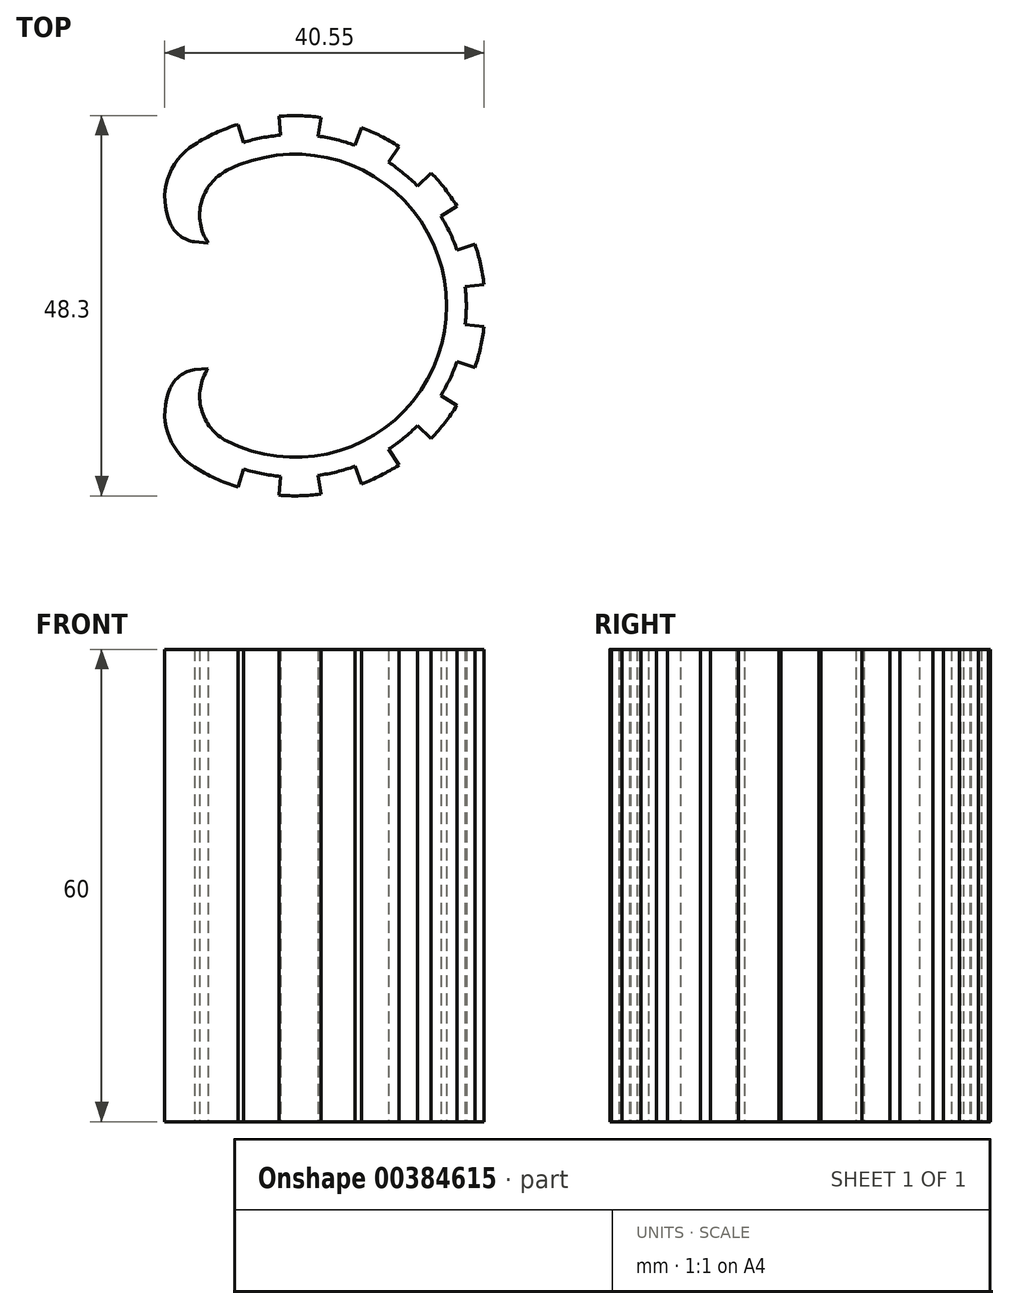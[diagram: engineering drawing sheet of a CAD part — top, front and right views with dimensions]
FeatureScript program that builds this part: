
annotation { "Feature Type Name" : "Feature", "Feature Type Description" : "" }
export const myFeature = defineFeature(function(context is Context, id is Id, definition is map)
    precondition{}
    {
        {
            var Q0;
            Q0=qCreatedBy(makeId("Top.planeOp"),FACE);
            var sketch = newSketch(context, id + "F0", { "sketchPlane" : qUnion([Q0])});
            skCircle(sketch, "E0", {"center": v(0, 0) * mm, "radius": 24.15 * mm, "construction": true});
            skCircle(sketch, "E1", {"center": v(0, 0) * mm, "radius": 19.25 * mm, "construction": true});
            skCircle(sketch, "E2", {"center": v(0, 0) * mm, "radius": 21.75 * mm, "construction": true});
            skLineSegment(sketch, "E3", {"start": v(24.15, -24.78) * mm, "end": v(24.15, 24.83) * mm, "construction": true});
            skLineSegment(sketch, "E4", {"start": v(-27.29, 0) * mm, "end": v(29.37, 0) * mm, "construction": true});
            skLineSegment(sketch, "E5.0", {"start": v(-27.29, -7.7) * mm, "end": v(29.37, -7.7) * mm, "construction": true});
            skLineSegment(sketch, "E6.0", {"start": v(-27.29, 7.7) * mm, "end": v(29.37, 7.7) * mm, "construction": true});
            skLineSegment(sketch, "E7", {"start": v(-7.9, 7.7) * mm, "end": v(-30.03, 9.64) * mm, "construction": true});
            skLineSegment(sketch, "E8", {"start": v(-9.96, -7.7) * mm, "end": v(-30.2, -9.47) * mm, "construction": true});
            skLineSegment(sketch, "E9", {"start": v(-7.25, 14.43) * mm, "end": v(-7.25, 0) * mm, "construction": true});
            skLineSegment(sketch, "E10", {"start": v(-7.25, 0) * mm, "end": v(-7.25, -27.12) * mm, "construction": true});
            skLineSegment(sketch, "E11.0", {"start": v(-16.55, -24.78) * mm, "end": v(-16.55, 24.83) * mm, "construction": true});
            skLineSegment(sketch, "E12.0", {"start": v(-11.05, -24.78) * mm, "end": v(-11.05, 24.83) * mm, "construction": true});
            skCircle(sketch, "E13", {"center": v(-8.55, 13.7) * mm, "radius": 8 * mm, "construction": true});
            skCircle(sketch, "E14", {"center": v(-12.21, 12.1) * mm, "radius": 4 * mm, "construction": true});
            skPoint(sketch, "E15", {"position": v(-11.05, 7.98) * mm});
            skCircle(sketch, "E16.MirrorC", {"center": v(-8.55, -13.7) * mm, "radius": 8 * mm, "construction": true});
            skCircle(sketch, "E17.MirrorC", {"center": v(-12.21, -12.1) * mm, "radius": 4 * mm, "construction": true});
            skArc(sketch, "E18.MirrorCS", {"start": v(-8.64, -17.2) * mm, "mid": v(-11.28, -12.96) * mm, "end": v(-11.05, -7.98) * mm, "construction": true});
            skArc(sketch, "E19", {"start": v(-8.57, 17.24) * mm, "mid": v(-11.9, 13.17) * mm, "end": v(-11.05, 7.98) * mm, "construction": true});
            skSolve(sketch);
        }
        {
            var Q0;
            Q0=qCreatedBy(makeId("Top.planeOp"),FACE);
            var sketch = newSketch(context, id + "F1", { "sketchPlane" : qUnion([Q0])});
            skLineSegment(sketch, "E20", {"start": v(0, 0) * mm, "end": v(-10.1, 32.05) * mm, "construction": true});
            skPoint(sketch, "E21.center", {"position": v(0, 0) * mm});
            skLineSegment(sketch, "E22.1.0", {"start": v(0, 0) * mm, "end": v(33.61, 0) * mm, "construction": true});
            skLineSegment(sketch, "E22.2.0", {"start": v(0, 0) * mm, "end": v(-10.1, -32.05) * mm, "construction": true});
            skSolve(sketch);
        }
        {
            var Q0;
            Q0=qCreatedBy(makeId("Top.planeOp"),FACE);
            var sketch = newSketch(context, id + "F2", { "sketchPlane" : qUnion([Q0])});
            skLineSegment(sketch, "E23", {"start": v(-6.55, 20.74) * mm, "end": v(-7.26, 23.03) * mm});
            skLineSegment(sketch, "E24.1.0", {"start": v(-1.85, 21.67) * mm, "end": v(-2.04, 24.06) * mm});
            skLineSegment(sketch, "E24.2.0", {"start": v(2.94, 21.55) * mm, "end": v(3.28, 23.93) * mm});
            skLineSegment(sketch, "E24.3.0", {"start": v(7.59, 20.38) * mm, "end": v(8.43, 22.63) * mm});
            skLineSegment(sketch, "E24.4.0", {"start": v(11.86, 18.23) * mm, "end": v(13.18, 20.23) * mm});
            skLineSegment(sketch, "E24.5.0", {"start": v(15.57, 15.19) * mm, "end": v(17.3, 16.86) * mm});
            skLineSegment(sketch, "E24.6.0", {"start": v(18.52, 11.41) * mm, "end": v(20.57, 12.66) * mm});
            skLineSegment(sketch, "E24.7.0", {"start": v(20.57, 7.08) * mm, "end": v(22.84, 7.85) * mm});
            skLineSegment(sketch, "E24.8.0", {"start": v(21.62, 2.4) * mm, "end": v(24, 2.66) * mm});
            skLineSegment(sketch, "E24.9.0", {"start": v(21.62, -2.38) * mm, "end": v(24, -2.66) * mm});
            skLineSegment(sketch, "E24.10.0", {"start": v(20.57, -7.06) * mm, "end": v(22.84, -7.85) * mm});
            skLineSegment(sketch, "E24.11.0", {"start": v(18.53, -11.4) * mm, "end": v(20.57, -12.66) * mm});
            skLineSegment(sketch, "E24.12.0", {"start": v(15.58, -15.17) * mm, "end": v(17.3, -16.86) * mm});
            skLineSegment(sketch, "E24.13.0", {"start": v(11.88, -18.22) * mm, "end": v(13.18, -20.23) * mm});
            skLineSegment(sketch, "E24.14.0", {"start": v(7.6, -20.38) * mm, "end": v(8.43, -22.63) * mm});
            skLineSegment(sketch, "E24.15.0", {"start": v(2.96, -21.55) * mm, "end": v(3.28, -23.93) * mm});
            skLineSegment(sketch, "E24.16.0", {"start": v(-1.83, -21.67) * mm, "end": v(-2.04, -24.06) * mm});
            skLineSegment(sketch, "E24.17.0", {"start": v(-6.53, -20.75) * mm, "end": v(-7.26, -23.03) * mm});
            skPoint(sketch, "E24.center", {"position": v(0, 0) * mm});
            skLineSegment(sketch, "E24.anchor1", {"start": v(0, 0) * mm, "end": v(-6.55, 20.74) * mm, "construction": true});
            skLineSegment(sketch, "E24.anchor2", {"start": v(0, 0) * mm, "end": v(-6.53, -20.75) * mm, "construction": true});
            skArc(sketch, "E25", {"start": v(19.25, 0) * mm, "mid": v(10.11, 16.38) * mm, "end": v(-8.63, 17.2) * mm});
            skArc(sketch, "E26", {"start": v(-8.63, 17.2) * mm, "mid": v(-11.9, 13.13) * mm, "end": v(-11.05, 7.98) * mm});
            skArc(sketch, "E27", {"start": v(-12.79, 20.49) * mm, "mid": v(-16.2, 16.06) * mm, "end": v(-15.87, 10.48) * mm});
            skArc(sketch, "E28", {"start": v(-15.87, 10.48) * mm, "mid": v(-14.62, 8.9) * mm, "end": v(-12.74, 8.13) * mm});
            skLineSegment(sketch, "E29", {"start": v(-12.74, 8.13) * mm, "end": v(-11.05, 7.98) * mm});
            skArc(sketch, "E30", {"start": v(-12.79, 20.49) * mm, "mid": v(-10.1, 21.93) * mm, "end": v(-7.26, 23.03) * mm});
            skArc(sketch, "E31", {"start": v(-6.55, 20.74) * mm, "mid": v(-4.23, 21.34) * mm, "end": v(-1.85, 21.67) * mm});
            skArc(sketch, "E32", {"start": v(2.94, 21.55) * mm, "mid": v(5.3, 21.1) * mm, "end": v(7.59, 20.38) * mm});
            skArc(sketch, "E33", {"start": v(3.28, 23.93) * mm, "mid": v(0.62, 24.14) * mm, "end": v(-2.04, 24.06) * mm});
            skArc(sketch, "E34", {"start": v(8.43, 22.63) * mm, "mid": v(10.88, 21.56) * mm, "end": v(13.18, 20.23) * mm});
            skArc(sketch, "E35", {"start": v(11.86, 18.23) * mm, "mid": v(13.8, 16.81) * mm, "end": v(15.57, 15.19) * mm});
            skArc(sketch, "E36", {"start": v(17.3, 16.86) * mm, "mid": v(19.05, 14.85) * mm, "end": v(20.57, 12.66) * mm});
            skArc(sketch, "E37", {"start": v(18.52, 11.41) * mm, "mid": v(19.66, 9.3) * mm, "end": v(20.57, 7.08) * mm});
            skArc(sketch, "E38", {"start": v(22.84, 7.85) * mm, "mid": v(23.56, 5.29) * mm, "end": v(24, 2.66) * mm});
            skArc(sketch, "E39", {"start": v(21.62, 2.4) * mm, "mid": v(21.72, 1.2) * mm, "end": v(21.75, 0) * mm});
            skArc(sketch, "E40.MirrorCS", {"start": v(21.62, -2.4) * mm, "mid": v(21.72, -1.2) * mm, "end": v(21.75, 0) * mm});
            skLineSegment(sketch, "E41.MirrorCS", {"start": v(21.62, -2.4) * mm, "end": v(24, -2.66) * mm});
            skArc(sketch, "E42.MirrorCS", {"start": v(22.84, -7.85) * mm, "mid": v(23.56, -5.29) * mm, "end": v(24, -2.66) * mm});
            skLineSegment(sketch, "E43.MirrorCS", {"start": v(20.57, -7.08) * mm, "end": v(22.84, -7.85) * mm});
            skArc(sketch, "E44.MirrorCS", {"start": v(18.52, -11.41) * mm, "mid": v(19.66, -9.3) * mm, "end": v(20.57, -7.08) * mm});
            skLineSegment(sketch, "E45.MirrorCS", {"start": v(18.52, -11.41) * mm, "end": v(20.57, -12.66) * mm});
            skArc(sketch, "E46.MirrorCS", {"start": v(17.3, -16.86) * mm, "mid": v(19.05, -14.85) * mm, "end": v(20.57, -12.66) * mm});
            skLineSegment(sketch, "E47.MirrorCS", {"start": v(15.57, -15.19) * mm, "end": v(17.3, -16.86) * mm});
            skArc(sketch, "E48.MirrorCS", {"start": v(11.86, -18.23) * mm, "mid": v(13.8, -16.81) * mm, "end": v(15.57, -15.19) * mm});
            skLineSegment(sketch, "E49.MirrorCS", {"start": v(11.86, -18.23) * mm, "end": v(13.18, -20.23) * mm});
            skArc(sketch, "E50.MirrorCS", {"start": v(8.43, -22.63) * mm, "mid": v(10.88, -21.56) * mm, "end": v(13.18, -20.23) * mm});
            skLineSegment(sketch, "E51.MirrorCS", {"start": v(7.59, -20.38) * mm, "end": v(8.43, -22.63) * mm});
            skArc(sketch, "E52.MirrorCS", {"start": v(2.94, -21.55) * mm, "mid": v(5.3, -21.1) * mm, "end": v(7.59, -20.38) * mm});
            skLineSegment(sketch, "E53.MirrorCS", {"start": v(2.94, -21.55) * mm, "end": v(3.28, -23.93) * mm});
            skArc(sketch, "E54.MirrorCS", {"start": v(3.28, -23.93) * mm, "mid": v(0.62, -24.14) * mm, "end": v(-2.04, -24.06) * mm});
            skLineSegment(sketch, "E55.MirrorCS", {"start": v(-1.85, -21.67) * mm, "end": v(-2.04, -24.06) * mm});
            skArc(sketch, "E56.MirrorCS", {"start": v(-6.55, -20.74) * mm, "mid": v(-4.23, -21.34) * mm, "end": v(-1.85, -21.67) * mm});
            skLineSegment(sketch, "E57.MirrorCS", {"start": v(-6.55, -20.74) * mm, "end": v(-7.26, -23.03) * mm});
            skArc(sketch, "E58.MirrorCS", {"start": v(-12.79, -20.49) * mm, "mid": v(-10.1, -21.93) * mm, "end": v(-7.26, -23.03) * mm});
            skArc(sketch, "E59.MirrorCS", {"start": v(-12.79, -20.49) * mm, "mid": v(-16.2, -16.06) * mm, "end": v(-15.87, -10.48) * mm});
            skArc(sketch, "E60.MirrorCS", {"start": v(-15.87, -10.48) * mm, "mid": v(-14.62, -8.9) * mm, "end": v(-12.74, -8.13) * mm});
            skLineSegment(sketch, "E61.MirrorCS", {"start": v(-12.74, -8.13) * mm, "end": v(-11.05, -7.98) * mm});
            skArc(sketch, "E62.MirrorCS", {"start": v(-8.63, -17.2) * mm, "mid": v(-11.9, -13.13) * mm, "end": v(-11.05, -7.98) * mm});
            skArc(sketch, "E63.MirrorCS", {"start": v(19.25, 0) * mm, "mid": v(10.11, -16.38) * mm, "end": v(-8.63, -17.2) * mm});
            skSolve(sketch);
        }
        {
            var Q0;
            Q0 = qSketchRegion(id + "F2", true);
            extrude(context, id + "F3", {"entities" : qUnion([Q0]), "endBound" : BoundingType.SYMMETRIC, "depth" : 60 * mm});
        }
    });
